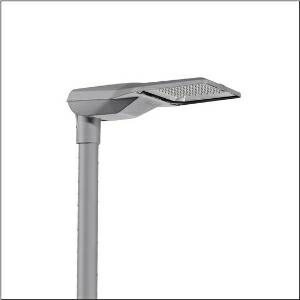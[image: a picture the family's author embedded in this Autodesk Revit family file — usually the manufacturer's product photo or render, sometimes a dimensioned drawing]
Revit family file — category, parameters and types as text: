
# Revit family: streetlight_sl_21_iq_midi___p0_5a_5xe3v31g08mb_4daf
name_source: partatom
category: Lighting Fixtures
units: mm (PartAtom-declared; Revit-internal decimal feet)

## family parameters
Cut with Voids When Loaded = No
Host = Face
Light Source = No
Part Type = Normal
Room Calculation Point = No
Round Connector Dimension = Use Diameter
Shared = No

## types (1)
- --- (1 x LED, 19170 lm, 146.7 W, 3000K)
    Apparent Load = 147 VA
    CIE Flux Codes = 37 73 96 100 100
    Color Rendering = 70
    Color Temperature = 3000K
    Default Elevation = 1800 mm
    Description = Streetlight SL 21 iQ midi, mast luminaire, primary light control with lens, of PMMA, primary optical cover: cover, of toughened safety glass, transparent, light distribution: P0.5a, light emission: direct distribution, primary light characteristic: asymmetric, installation type: post-top, side-entry, LED, High Power LED, rated luminous flux: 19.170lm, luminous efficacy: 131lm/W, light colour: 730, colour temperature: 3000K, control gear: iQ Street-Remote, control: pre-setting: linear dimming characteristic, Street-Remote, Auto-Match, Temp-Guard, Lumen-Switch, Night-Set, Smart-Wire, Light-Fading, Desk-Remote (wireless, voltage-free reading and setting of iQ features in the workshop via application-optimized NFC function/RFID function), optimised constant luminous flux control (CLO 2.0), mains connection: 230..240V, AC, 50/60Hz, start of lifetime: 147W, end of service life: 161W, reduction: 62W, luminaire housing, of diecast aluminium, powder-coated, SITECO metallic grey (DB 702S), corrosivity category C5 high according to DIN EN ISO 12944, please order mast flange separately, inclination adjustable: 0°, 5°, 10°, 15°, sealing non-destructively replaceable, multi-level sealing system, length: 644mm, width: 335mm, height: 110mm, mast flange for spigot size: 42mm (side-entry): 5XC10008XM4, 60/48mm (side-entry/post-top): 5XC10108XM2, 76/60mm (side-entry/post-top): 5XC10108XM1, mounting height: 4..8m, protection rating (complete): IP66, insulation class (complete): insulation class II (safety insulation), certification: CE, ENEC, ENEC+, VDE, impact resistance: IK10, permissible operating ambient temperature for outdoor applications: -40..+50°C, standard-compliant lighting for roads and squares, packaging unit: 1 piece

Light Distribution: P0.5a
    Height = 111 mm
    Lamp = 1 x LED
    Lamp Light Flux = 19170 lm
    Lamp Power = 146.7 W
    Lamp count = 1
    Length = 644 mm
    Luminous efficacy = 131 lm/W
    Manufacturer = Siteco
    ModVariant = No
    Model = 5XE3V31G08MB
    Number of Poles = 1
    OnlyDefault = Yes
    Power Factor = 1
    Product Name = Streetlight SL 21 iQ midi | P0.5a
    Product group = mast luminaire | pylon top
    ProductGroupID = 6100
    Protection Class = Protection class II
    Protection Degree = IP 66
    RLX_Detail_Level = 1
    RLX_Emergency_Light_Flux = 0 lm
    RLX_Emergency_Type = 0
    RLX_Emergency_Type_DB = No
    RlxData = <blob elided: 90029 chars, md5=1c71602d>
    Socket = socket
    Standby Power = 0 W
    System Light Flux = 19169 lm
    System Power = 147 W
    Type Comments = factory setting: luminous flux: 100 % | dim-lin: 254 | 753 mA
    Type Image = l_1004298.jpg
    URL = http://relux.com
    VarID = @adj_077357
    Voltage = 0 V
    Weight = 0.00 kg
    Width = 336 mm

## geometry (parser evidence)
native form markers: Blend x4, Sweep x10
no freeform markers — native parametric forms only
